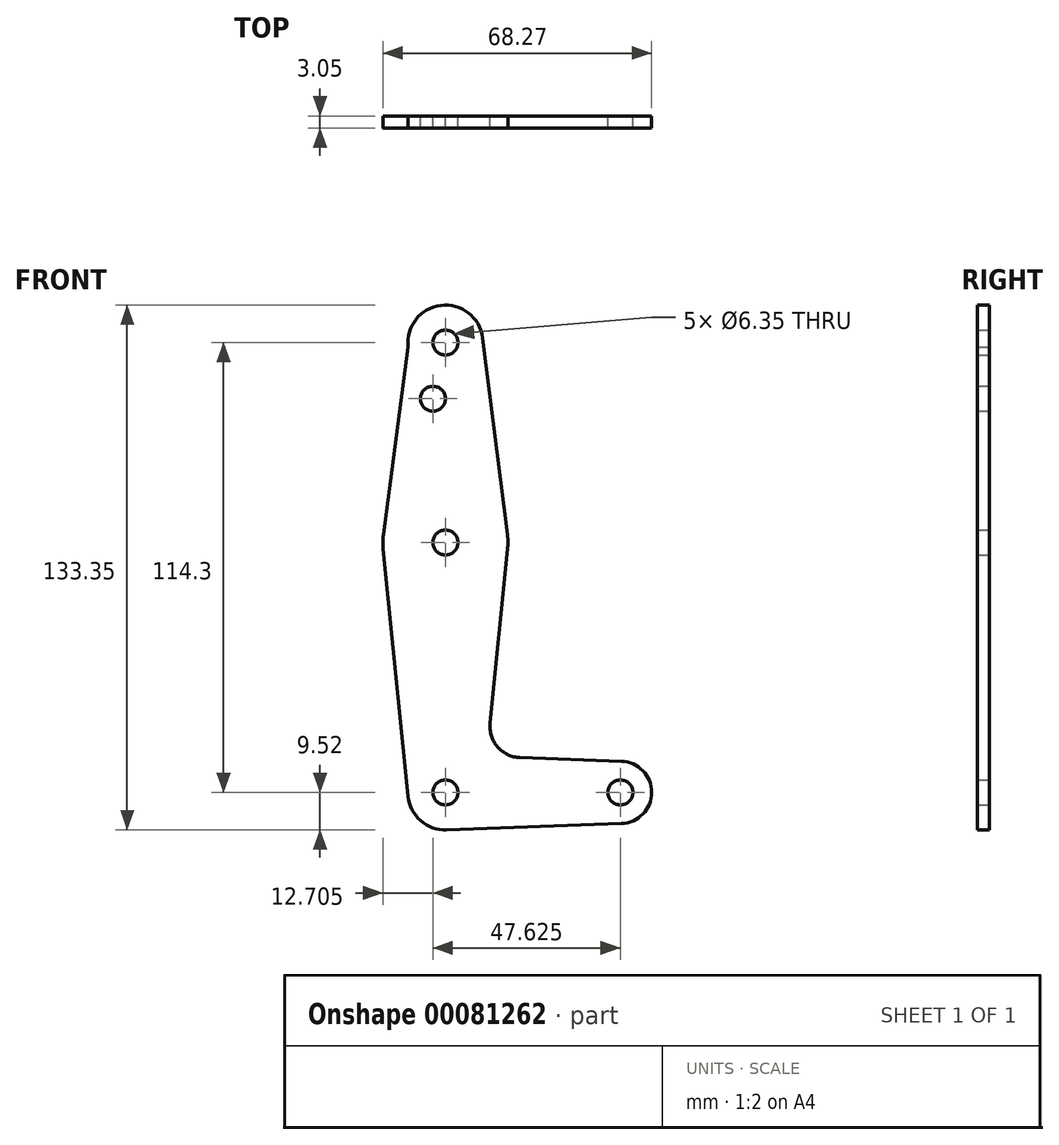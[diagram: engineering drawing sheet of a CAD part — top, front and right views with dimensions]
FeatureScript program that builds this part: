
annotation { "Feature Type Name" : "Feature", "Feature Type Description" : "" }
export const myFeature = defineFeature(function(context is Context, id is Id, definition is map)
    precondition{}
    {
        {
            var Q0;
            Q0=qCreatedBy(makeId("Front.planeOp"),FACE);
            var sketch = newSketch(context, id + "F0", { "sketchPlane" : qUnion([Q0])});
            skLineSegment(sketch, "E0", {"start": v(0, 0) * mm, "end": v(0, 114.3) * mm, "construction": true});
            skLineSegment(sketch, "E1", {"start": v(0, 0) * mm, "end": v(44.45, 0) * mm, "construction": true});
            skCircle(sketch, "E2", {"center": v(0, 114.3) * mm, "radius": 9.53 * mm});
            skCircle(sketch, "E3", {"center": v(0, 63.5) * mm, "radius": 15.88 * mm});
            skCircle(sketch, "E4", {"center": v(0, 0) * mm, "radius": 9.53 * mm});
            skCircle(sketch, "E5", {"center": v(44.45, 0) * mm, "radius": 7.94 * mm});
            skCircle(sketch, "E6", {"center": v(0, 114.3) * mm, "radius": 3.18 * mm});
            skCircle(sketch, "E7", {"center": v(0, 63.5) * mm, "radius": 3.18 * mm});
            skCircle(sketch, "E8", {"center": v(0, 0) * mm, "radius": 3.18 * mm});
            skCircle(sketch, "E9", {"center": v(44.45, 0) * mm, "radius": 3.18 * mm});
            skCircle(sketch, "E10", {"center": v(-3.18, 100.03) * mm, "radius": 3.18 * mm});
            skLineSegment(sketch, "E11", {"start": v(-9.46, 113.17) * mm, "end": v(-15.74, 65.58) * mm});
            skLineSegment(sketch, "E12", {"start": v(15.8, 61.91) * mm, "end": v(11.34, 17.6) * mm});
            skLineSegment(sketch, "E13", {"start": v(0.34, -9.52) * mm, "end": v(44.73, -7.93) * mm});
            skLineSegment(sketch, "E14", {"start": v(18.97, 8.85) * mm, "end": v(44.73, 7.93) * mm});
            skArc(sketch, "E15.filletArc", {"start": v(11.34, 17.6) * mm, "mid": v(13.26, 11.57) * mm, "end": v(18.97, 8.85) * mm});
            skLineSegment(sketch, "E16", {"start": v(9.45, 115.5) * mm, "end": v(15.75, 65.48) * mm});
            skLineSegment(sketch, "E17", {"start": v(-15.8, 61.91) * mm, "end": v(-9.48, -0.95) * mm});
            skSolve(sketch);
        }
        {
            var Q0;
            Q0=makeQuery(id+"F0.imprint","IMPRINT",FACE,{"disambiguationData":[TD([[makeQuery(id+"F0.imprint","IMPRINT",EDGE,{"derivedFrom":sQuery(id+"F0.wireOp",EDGE,"E10")}),-1.0]])]});
            var Q1;
            Q1=makeQuery(id+"F0.imprint","IMPRINT",FACE,{"disambiguationData":[TD([[makeQuery(id+"F0.imprint","IMPRINT",EDGE,{"derivedFrom":sQuery(id+"F0.wireOp",EDGE,"E6")}),-1.0]])]});
            var Q2;
            Q2=makeQuery(id+"F0.imprint","IMPRINT",FACE,{"disambiguationData":[TD([[makeQuery(id+"F0.imprint","IMPRINT",EDGE,{"derivedFrom":sQuery(id+"F0.wireOp",EDGE,"E7")}),-1.0]])]});
            var Q3;
            {var subQ0=sQuery(id+"F0.wireOp",EDGE,"E12");Q3=makeQuery(id+"F0.imprint","IMPRINT",FACE,{"disambiguationData":[TD([[makeQuery(id+"F0.imprint","IMPRINT",EDGE,{"derivedFrom":subQ0}),-1.0]])]});}
            var Q4;
            Q4=makeQuery(id+"F0.imprint","IMPRINT",FACE,{"disambiguationData":[TD([[makeQuery(id+"F0.imprint","IMPRINT",EDGE,{"derivedFrom":sQuery(id+"F0.wireOp",EDGE,"E8")}),-1.0]])]});
            var Q5;
            Q5=makeQuery(id+"F0.imprint","IMPRINT",FACE,{"disambiguationData":[TD([[makeQuery(id+"F0.imprint","IMPRINT",EDGE,{"derivedFrom":sQuery(id+"F0.wireOp",EDGE,"E9")}),-1.0]])]});
            extrude(context, id + "F1", {"entities" : qUnion([Q0, Q1, Q2, Q3, Q4, Q5]), "depth" : 3.05 * mm});
        }
    });
